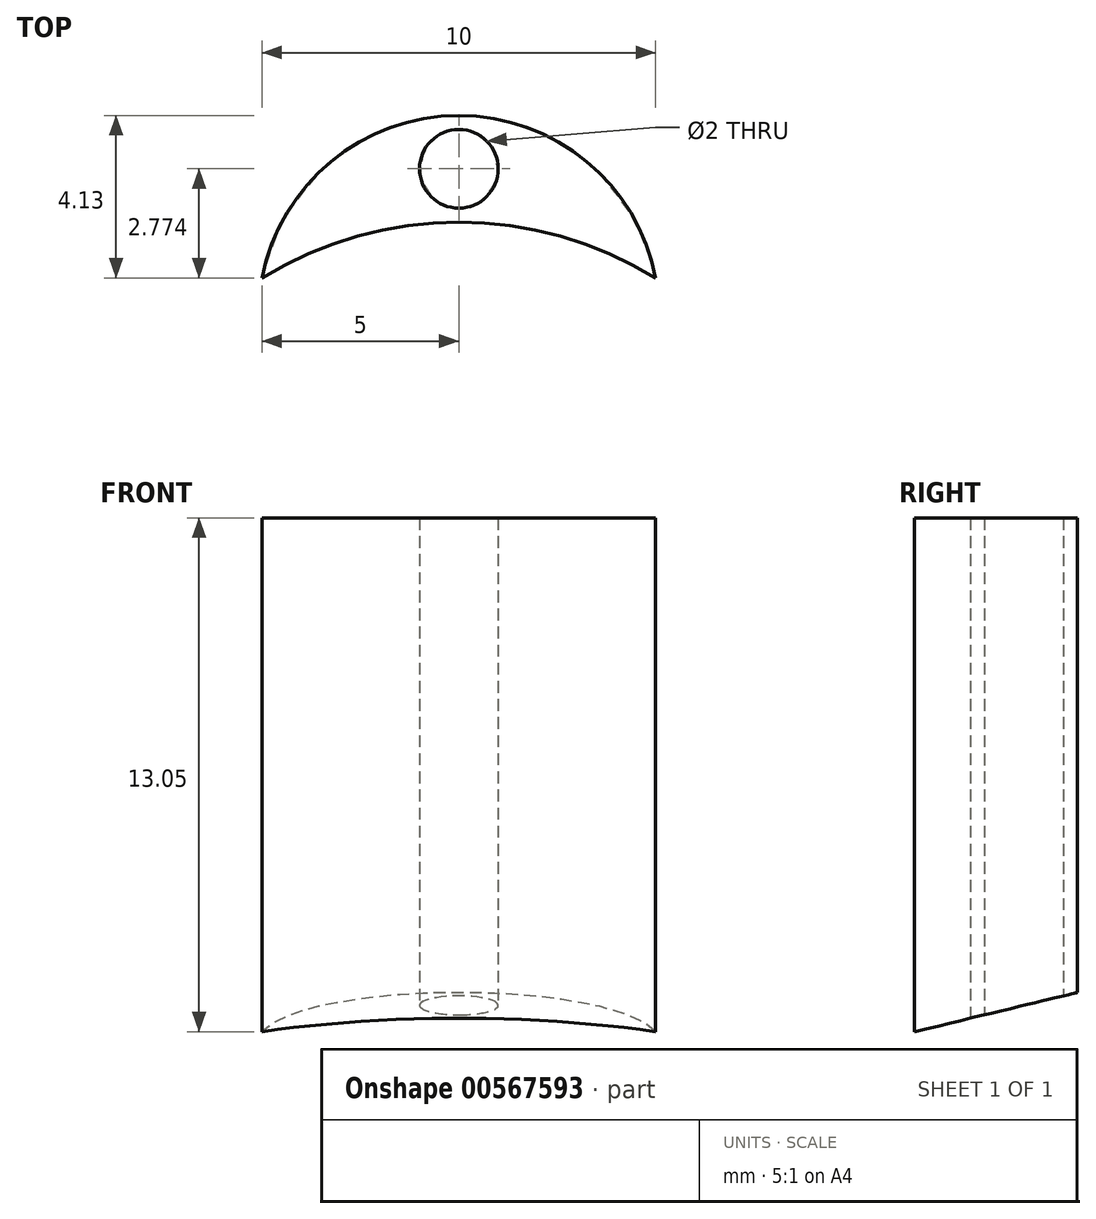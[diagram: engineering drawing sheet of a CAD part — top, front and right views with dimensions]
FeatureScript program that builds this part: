
annotation { "Feature Type Name" : "Feature", "Feature Type Description" : "" }
export const myFeature = defineFeature(function(context is Context, id is Id, definition is map)
    precondition{}
    {
        {
            var Q0;
            Q0=qCreatedBy(makeId("Top.planeOp"),FACE);
            var sketch = newSketch(context, id + "F0", { "sketchPlane" : qUnion([Q0])});
            skCircle(sketch, "E0", {"center": v(0, 0) * mm, "radius": 9.5 * mm});
            skArc(sketch, "E1", {"start": v(5, 8.08) * mm, "mid": v(0, 12.2) * mm, "end": v(-5, 8.08) * mm});
            skCircle(sketch, "E2", {"center": v(0, 10.85) * mm, "radius": 1 * mm});
            skSolve(sketch);
        }
        {
            var Q0;
            Q0=qCreatedBy(makeId("Top.planeOp"),FACE);
            var sketch = newSketch(context, id + "F1", { "sketchPlane" : qUnion([Q0])});
            skLineSegment(sketch, "E3", {"start": v(0, 0) * mm, "end": v(5, 0) * mm});
            skLineSegment(sketch, "E4", {"start": v(5, 0) * mm, "end": v(5, 20) * mm});
            skLineSegment(sketch, "E5", {"start": v(5, 20) * mm, "end": v(15, 20) * mm});
            skLineSegment(sketch, "E6", {"start": v(15, 20) * mm, "end": v(15, -15) * mm});
            skLineSegment(sketch, "E7", {"start": v(15, -15) * mm, "end": v(-15, -15) * mm});
            skLineSegment(sketch, "E8", {"start": v(-15, -15) * mm, "end": v(-15, 20) * mm});
            skLineSegment(sketch, "E9", {"start": v(-15, 20) * mm, "end": v(-5, 20) * mm});
            skLineSegment(sketch, "E10", {"start": v(-5, 20) * mm, "end": v(-5, 0) * mm});
            skLineSegment(sketch, "E11", {"start": v(-5, 0) * mm, "end": v(0, 0) * mm});
            skCircle(sketch, "E12", {"center": v(0, 0) * mm, "radius": 9.5 * mm});
            skSolve(sketch);
        }
        {
            var Q0;
            Q0 = qSketchRegion(id + "F0", true);
            extrude(context, id + "F2", {"entities" : qUnion([Q0]), "depth" : 15 * mm, "offsetDistance" : 25 * mm});
        }
        {
            var Q0;
            Q0 = qSketchRegion(id + "F1", true);
            extrude(context, id + "F3", {"entities" : qUnion([Q0]), "operationType" : NewBodyOperationType.REMOVE, "endBound" : BoundingType.THROUGH_ALL, "depth" : 25 * mm, "offsetDistance" : 25 * mm});
        }
        {
            var Q0;
            Q0=qCreatedBy(makeId("Right.planeOp"),FACE);
            var sketch = newSketch(context, id + "F4", { "sketchPlane" : qUnion([Q0])});
            skLineSegment(sketch, "E13", {"start": v(0, 0) * mm, "end": v(17.09, 4.12) * mm});
            skLineSegment(sketch, "E14", {"start": v(17.09, 4.12) * mm, "end": v(17.09, 0) * mm});
            skLineSegment(sketch, "E15", {"start": v(17.09, 0) * mm, "end": v(0, 0) * mm});
            skSolve(sketch);
        }
        {
            var Q0;
            Q0=makeQuery(id+"F4.imprint","IMPRINT",FACE,{"disambiguationData":[TD([[makeQuery(id+"F4.imprint","IMPRINT",EDGE,{"derivedFrom":sQuery(id+"F4.wireOp",EDGE,"E13")}),-1.0]])]});
            var Q1;
            Q1=sQuery(id+"F4.wireOp",EDGE,"E13");
            extrude(context, id + "F5", {"entities" : qUnion([Q0]), "operationType" : NewBodyOperationType.REMOVE, "surfaceEntities" : qUnion([Q1]), "endBound" : BoundingType.THROUGH_ALL, "depth" : 25 * mm, "offsetDistance" : 25 * mm, "hasSecondDirection" : true, "secondDirectionBound" : SecondDirectionBoundingType.THROUGH_ALL, "secondDirectionOppositeDirection" : true, "secondDirectionDepth" : 25 * mm});
        }
    });
